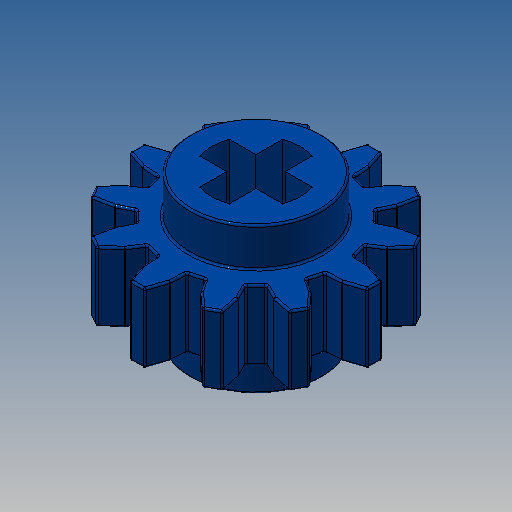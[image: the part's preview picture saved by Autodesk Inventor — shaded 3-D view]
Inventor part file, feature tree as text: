
AUTODESK INVENTOR PART (.ipt)
format: ipt  version: 2025 (Build 290162010, 162A)  size: 664,576 bytes
history: native  units: in
note: dims shown in document units (in); Inventor stores cm internally (conversion verified against a paired STEP export)
features: extrude x3, fillet x2, sketch x1, pattern_circular x1
ambient origin geometry x8: Origin, YZ Plane, XZ Plane, XY Plane, X Axis, Y Axis, Z Axis, Center Point
bodies: Solid1 (feature_tree)
feature tree (7):
  sketch  "Sketch2"  dims[d1=0.189in d2=0.063in d3=0.0315in d4=0.2835in d9=0.2835in d11=0.0315in d12=0.0591in d13=0.063in d14=0.0413in d15=0.1496in d16=0.0in d17=0.315in d18=0.0in d19=0.1496in d20=0.0in d21=0.0039in d22=4.7244in d23=360.0deg d25=0.0039in d26=0.0in d27=0.0in d28=0.0in d29=0.2558in d30=0.0734in]
  extrude  "Extrusion1"  Depth=0.063in
  extrude  "Extrusion2"  Depth=0.0039in
  extrude  "Extrusion3"  Depth=0.0039in
  fillet  "Fillet1"  Radius=0.2835in
  pattern_circular  "Circular Pattern1"  [2 undecoded]
  fillet  "Fillet2"  Radius=0.0591in
note: 2 required parameter values undecoded (feature->parameter linkage not recoverable at this tier; creation-order binding heuristic only, values carry confidence <= 0.55)
